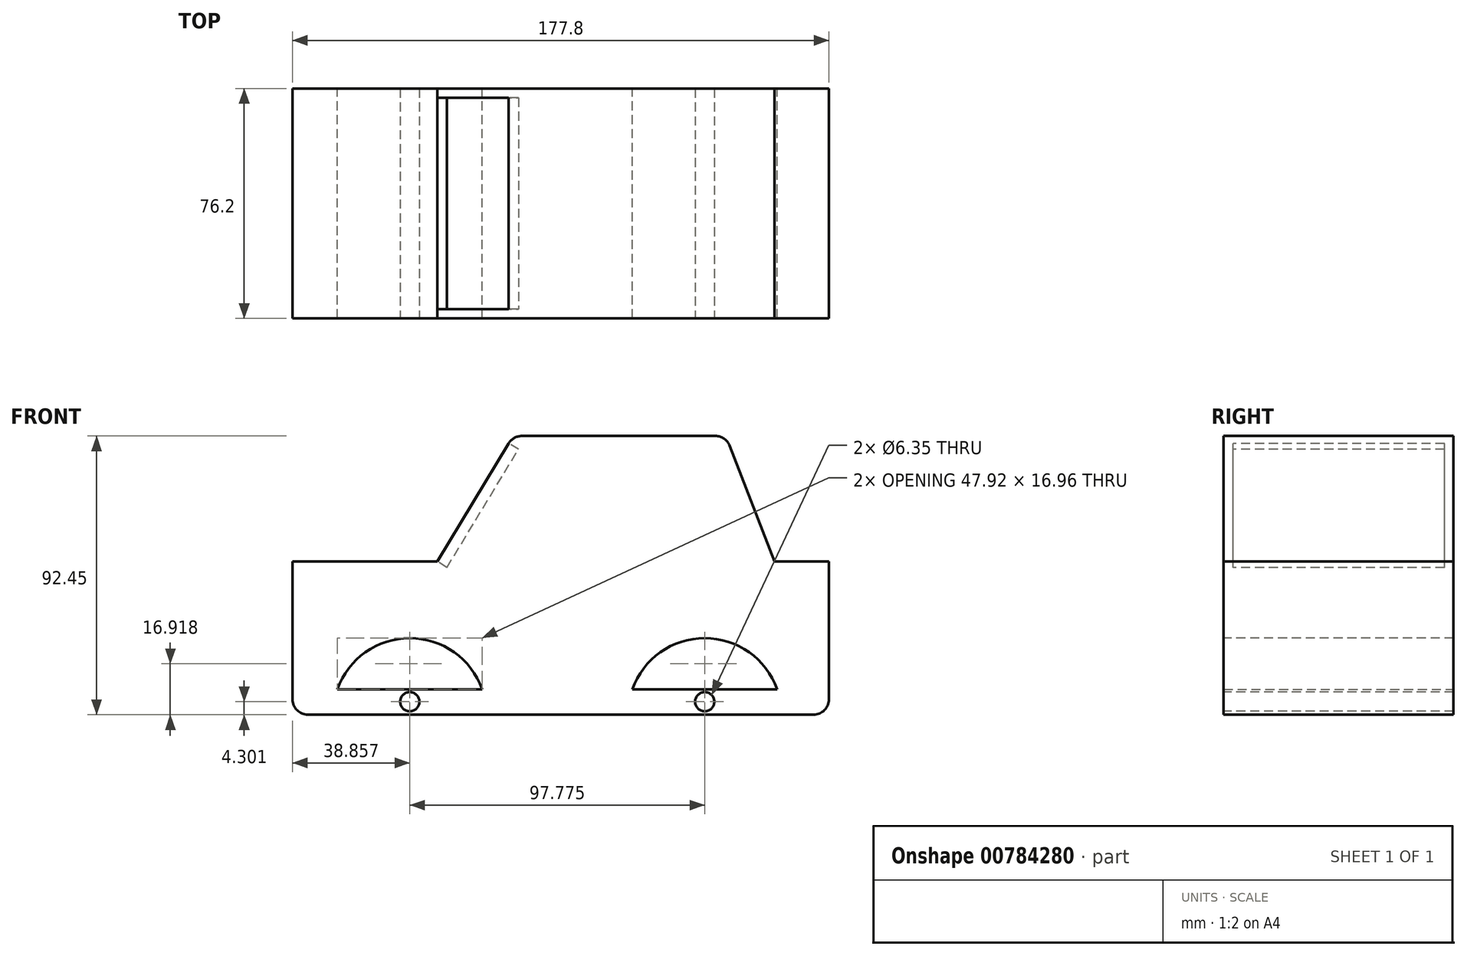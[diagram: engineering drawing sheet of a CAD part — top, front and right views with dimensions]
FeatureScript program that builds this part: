
annotation { "Feature Type Name" : "Feature", "Feature Type Description" : "" }
export const myFeature = defineFeature(function(context is Context, id is Id, definition is map)
    precondition{}
    {
        {
            var Q0;
            Q0=qCreatedBy(makeId("Top.planeOp"),FACE);
            var sketch = newSketch(context, id + "F0", { "sketchPlane" : qUnion([Q0])});
            skLineSegment(sketch, "E0.bottom", {"start": v(0, 0) * mm, "end": v(177.8, 0) * mm});
            skLineSegment(sketch, "E0.top", {"start": v(0, -76.2) * mm, "end": v(177.8, -76.2) * mm});
            skLineSegment(sketch, "E0.left", {"start": v(0, 0) * mm, "end": v(0, -76.2) * mm});
            skLineSegment(sketch, "E0.right", {"start": v(177.8, 0) * mm, "end": v(177.8, -76.2) * mm});
            skSolve(sketch);
        }
        {
            var Q0;
            Q0 = qSketchRegion(id + "F0", true);
            extrude(context, id + "F1", {"entities" : qUnion([Q0]), "depth" : 101.6 * mm, "offsetDistance" : 25.4 * mm});
        }
        {
            var Q0;
            Q0=makeQuery(id+"F1.opExtrude","SWEPT_FACE",FACE,{"disambiguationData":[OSD([sQuery(id+"F0.wireOp",EDGE,"E0.top")])]});
            var sketch = newSketch(context, id + "F2", { "sketchPlane" : qUnion([Q0])});
            skLineSegment(sketch, "E1", {"start": v(0, 50.8) * mm, "end": v(47.95, 50.8) * mm});
            skLineSegment(sketch, "E2", {"start": v(73.13, 92.45) * mm, "end": v(47.95, 50.8) * mm});
            skLineSegment(sketch, "E3", {"start": v(73.13, 92.45) * mm, "end": v(143.64, 92.45) * mm});
            skLineSegment(sketch, "E4", {"start": v(143.64, 92.45) * mm, "end": v(159.76, 50.8) * mm});
            skLineSegment(sketch, "E5", {"start": v(159.76, 50.8) * mm, "end": v(177.8, 50.8) * mm});
            skSolve(sketch);
        }
        {
            var Q0;
            {var subQ0=sQuery(id+"F2.wireOp",EDGE,"E1");Q0=makeQuery(id+"F2.imprint","IMPRINT",FACE,{"disambiguationData":[TD([[makeQuery(id+"F2.imprint","IMPRINT",EDGE,{"derivedFrom":subQ0}),1.0]])]});}
            extrude(context, id + "F3", {"entities" : qUnion([Q0]), "operationType" : NewBodyOperationType.REMOVE, "oppositeDirection" : true, "depth" : 203.2 * mm, "offsetDistance" : 25.4 * mm});
        }
        {
            var Q0;
            Q0=makeQuery(id+"F3.boolean.opBoolean","COPY",EDGE,{"derivedFrom":makeQuery(id+"F3.opExtrude","SWEPT_EDGE",EDGE,{"disambiguationData":[OSD([sQuery(id+"F0.wireOp",EDGE,"E0.top"),sQuery(id+"F0.wireOp",EDGE,"E0.left"),sQuery(id+"F2.wireOp",EDGE,"E1")])]})});
            var Q1;
            Q1=makeQuery(id+"F3.boolean.opBoolean","COPY",EDGE,{"derivedFrom":makeQuery(id+"F3.opExtrude","SWEPT_EDGE",EDGE,{"disambiguationData":[OSD([sQuery(id+"F2.wireOp",EDGE,"E2"),sQuery(id+"F2.wireOp",EDGE,"E3")])]})});
            var Q2;
            Q2=makeQuery(id+"F3.boolean.opBoolean","COPY",EDGE,{"derivedFrom":makeQuery(id+"F3.opExtrude","SWEPT_EDGE",EDGE,{"disambiguationData":[OSD([sQuery(id+"F2.wireOp",EDGE,"E3"),sQuery(id+"F2.wireOp",EDGE,"E4")])]})});
            var Q3;
            Q3=makeQuery(id+"F3.boolean.opBoolean","COPY",EDGE,{"derivedFrom":makeQuery(id+"F3.opExtrude","SWEPT_EDGE",EDGE,{"disambiguationData":[OSD([sQuery(id+"F0.wireOp",EDGE,"E0.top"),sQuery(id+"F0.wireOp",EDGE,"E0.right"),sQuery(id+"F2.wireOp",EDGE,"E5")])]})});
            var Q4;
            Q4=makeQuery(id+"F1.opExtrude","CAP_EDGE",EDGE,{"disambiguationData":[OSD([sQuery(id+"F0.wireOp",EDGE,"E0.right")])],"isStart":true});
            var Q5;
            Q5=makeQuery(id+"F1.opExtrude","CAP_EDGE",EDGE,{"disambiguationData":[OSD([sQuery(id+"F0.wireOp",EDGE,"E0.left")])],"isStart":true});
            fillet(context, id + "F4", {"entities" : qUnion([Q0, Q1, Q2, Q3, Q4, Q5]), "radius" : 5.08 * mm, "tangentPropagation" : true, "allowEdgeOverflow" : false});
        }
        {
            var Q0;
            Q0=makeQuery(id+"F3.boolean.opBoolean","COPY",FACE,{"derivedFrom":makeQuery(id+"F3.opExtrude","SWEPT_FACE",FACE,{"disambiguationData":[OSD([sQuery(id+"F2.wireOp",EDGE,"E2")])]})});
            var sketch = newSketch(context, id + "F5", { "sketchPlane" : qUnion([Q0])});
            skLineSegment(sketch, "E6.bottom", {"start": v(3.03, 68.28) * mm, "end": v(73.1, 68.28) * mm});
            skLineSegment(sketch, "E6.top", {"start": v(3.03, 114.08) * mm, "end": v(73.1, 114.08) * mm});
            skLineSegment(sketch, "E6.left", {"start": v(3.03, 68.28) * mm, "end": v(3.03, 114.08) * mm});
            skLineSegment(sketch, "E6.right", {"start": v(73.1, 68.28) * mm, "end": v(73.1, 114.08) * mm});
            skSolve(sketch);
        }
        {
            var Q0;
            Q0=makeQuery(id+"F5.imprint","IMPRINT",FACE,{"disambiguationData":[TD([[makeQuery(id+"F5.imprint","IMPRINT",EDGE,{"derivedFrom":sQuery(id+"F5.wireOp",EDGE,"E6.bottom")}),1.0]])]});
            extrude(context, id + "F6", {"entities" : qUnion([Q0]), "operationType" : NewBodyOperationType.REMOVE, "oppositeDirection" : true, "depth" : 3.8 * mm, "offsetDistance" : 25.4 * mm});
        }
        {
            var Q0;
            Q0=makeQuery(id+"F1.opExtrude","SWEPT_FACE",FACE,{"disambiguationData":[OSD([sQuery(id+"F0.wireOp",EDGE,"E0.top")])]});
            var sketch = newSketch(context, id + "F7", { "sketchPlane" : qUnion([Q0])});
            skArc(sketch, "E7", {"start": v(64.26, 0) * mm, "mid": v(38.86, 25.4) * mm, "end": v(13.46, 0) * mm});
            skArc(sketch, "E8", {"start": v(162.03, 0) * mm, "mid": v(136.63, 25.4) * mm, "end": v(111.23, 0) * mm});
            skLineSegment(sketch, "E9", {"start": v(5.08, 0) * mm, "end": v(172.72, 0) * mm});
            skSolve(sketch);
        }
        {
            var Q0;
            {var subQ0=sQuery(id+"F7.wireOp",EDGE,"E8");Q0=makeQuery(id+"F7.imprint","IMPRINT",FACE,{"disambiguationData":[TD([[makeQuery(id+"F7.imprint","IMPRINT",EDGE,{"derivedFrom":subQ0}),1.0]])]});}
            var Q1;
            {var subQ0=sQuery(id+"F7.wireOp",EDGE,"E7");Q1=makeQuery(id+"F7.imprint","IMPRINT",FACE,{"disambiguationData":[TD([[makeQuery(id+"F7.imprint","IMPRINT",EDGE,{"derivedFrom":subQ0}),1.0]])]});}
            extrude(context, id + "F8", {"entities" : qUnion([Q0, Q1]), "operationType" : NewBodyOperationType.REMOVE, "oppositeDirection" : true, "depth" : 203.2 * mm, "offsetDistance" : 25.4 * mm});
        }
        {
            var Q0;
            Q0=makeQuery(id+"F1.opExtrude","SWEPT_FACE",FACE,{"disambiguationData":[OSD([sQuery(id+"F0.wireOp",EDGE,"E0.bottom")])]});
            var sketch = newSketch(context, id + "F9", { "sketchPlane" : qUnion([Q0])});
            skLineSegment(sketch, "E10.bottom", {"start": v(-162.03, 0) * mm, "end": v(-111.23, 0) * mm});
            skLineSegment(sketch, "E10.top", {"start": v(-162.03, 0) * mm, "end": v(-111.23, 0) * mm});
            skLineSegment(sketch, "E10.left", {"start": v(-162.03, 0) * mm, "end": v(-162.03, 0) * mm});
            skLineSegment(sketch, "E10.right", {"start": v(-111.23, 0) * mm, "end": v(-111.23, 0) * mm});
            skLineSegment(sketch, "E11.bottom", {"start": v(-64.26, 0) * mm, "end": v(-13.46, 0) * mm});
            skLineSegment(sketch, "E11.top", {"start": v(-64.26, 0) * mm, "end": v(-13.46, 0) * mm});
            skLineSegment(sketch, "E11.left", {"start": v(-64.26, 0) * mm, "end": v(-64.26, 0) * mm});
            skLineSegment(sketch, "E11.right", {"start": v(-13.46, 0) * mm, "end": v(-13.46, 0) * mm});
            skArc(sketch, "E12", {"start": v(-111.23, 0) * mm, "mid": v(-111.6, 4.28) * mm, "end": v(-112.67, 8.44) * mm});
            skArc(sketch, "E13", {"start": v(-13.46, 0) * mm, "mid": v(-13.82, 4.28) * mm, "end": v(-14.9, 8.44) * mm});
            skLineSegment(sketch, "E14.top", {"start": v(-160.6, 8.44) * mm, "end": v(-112.67, 8.44) * mm});
            skLineSegment(sketch, "E15.top", {"start": v(-62.82, 8.44) * mm, "end": v(-14.9, 8.44) * mm});
            skArc(sketch, "E16.trimOffspring", {"start": v(-160.6, 8.44) * mm, "mid": v(-161.67, 4.28) * mm, "end": v(-162.03, 0) * mm});
            skPoint(sketch, "E17.orphan", {"position": v(-111.23, 8.44) * mm});
            skArc(sketch, "E18.trimOffspring", {"start": v(-62.82, 8.44) * mm, "mid": v(-63.9, 4.28) * mm, "end": v(-64.26, 0) * mm});
            skPoint(sketch, "E19.orphan", {"position": v(-13.46, 8.44) * mm});
            skSolve(sketch);
        }
        {
            var Q0;
            Q0 = qSketchRegion(id + "F9", true);
            extrude(context, id + "F10", {"entities" : qUnion([Q0]), "operationType" : NewBodyOperationType.ADD, "oppositeDirection" : true, "depth" : 76.2 * mm, "offsetDistance" : 25.4 * mm});
        }
        {
            var Q0;
            Q0=makeQuery(id+"F10.boolean.opBoolean","MERGE",FACE,{"derivedFrom":[makeQuery(id+"F1.opExtrude","SWEPT_FACE",FACE,{"disambiguationData":[OSD([sQuery(id+"F0.wireOp",EDGE,"E0.top")])]}),makeQuery(id+"F10.opExtrude","CAP_FACE",FACE,{"disambiguationData":[OSD([sQuery(id+"F9.wireOp",EDGE,"E12"),sQuery(id+"F9.wireOp",EDGE,"E10.bottom"),sQuery(id+"F9.wireOp",EDGE,"E14.top"),sQuery(id+"F9.wireOp",EDGE,"E16.trimOffspring")])],"isStart":false}),makeQuery(id+"F10.opExtrude","CAP_FACE",FACE,{"disambiguationData":[OSD([sQuery(id+"F9.wireOp",EDGE,"E13"),sQuery(id+"F9.wireOp",EDGE,"E11.bottom"),sQuery(id+"F9.wireOp",EDGE,"E15.top"),sQuery(id+"F9.wireOp",EDGE,"E18.trimOffspring")])],"isStart":false})]});
            var sketch = newSketch(context, id + "F11", { "sketchPlane" : qUnion([Q0])});
            skPoint(sketch, "E20", {"position": v(38.86, 8.44) * mm});
            skPoint(sketch, "E21", {"position": v(136.63, 8.44) * mm});
            skCircle(sketch, "E22", {"center": v(38.86, 4.3) * mm, "radius": 3.18 * mm});
            skCircle(sketch, "E23", {"center": v(136.63, 4.3) * mm, "radius": 3.18 * mm});
            skSolve(sketch);
        }
        {
            var Q0;
            Q0 = qSketchRegion(id + "F11", true);
            extrude(context, id + "F12", {"entities" : qUnion([Q0]), "operationType" : NewBodyOperationType.REMOVE, "oppositeDirection" : true, "depth" : 76.2 * mm, "offsetDistance" : 25.4 * mm});
        }
    });
